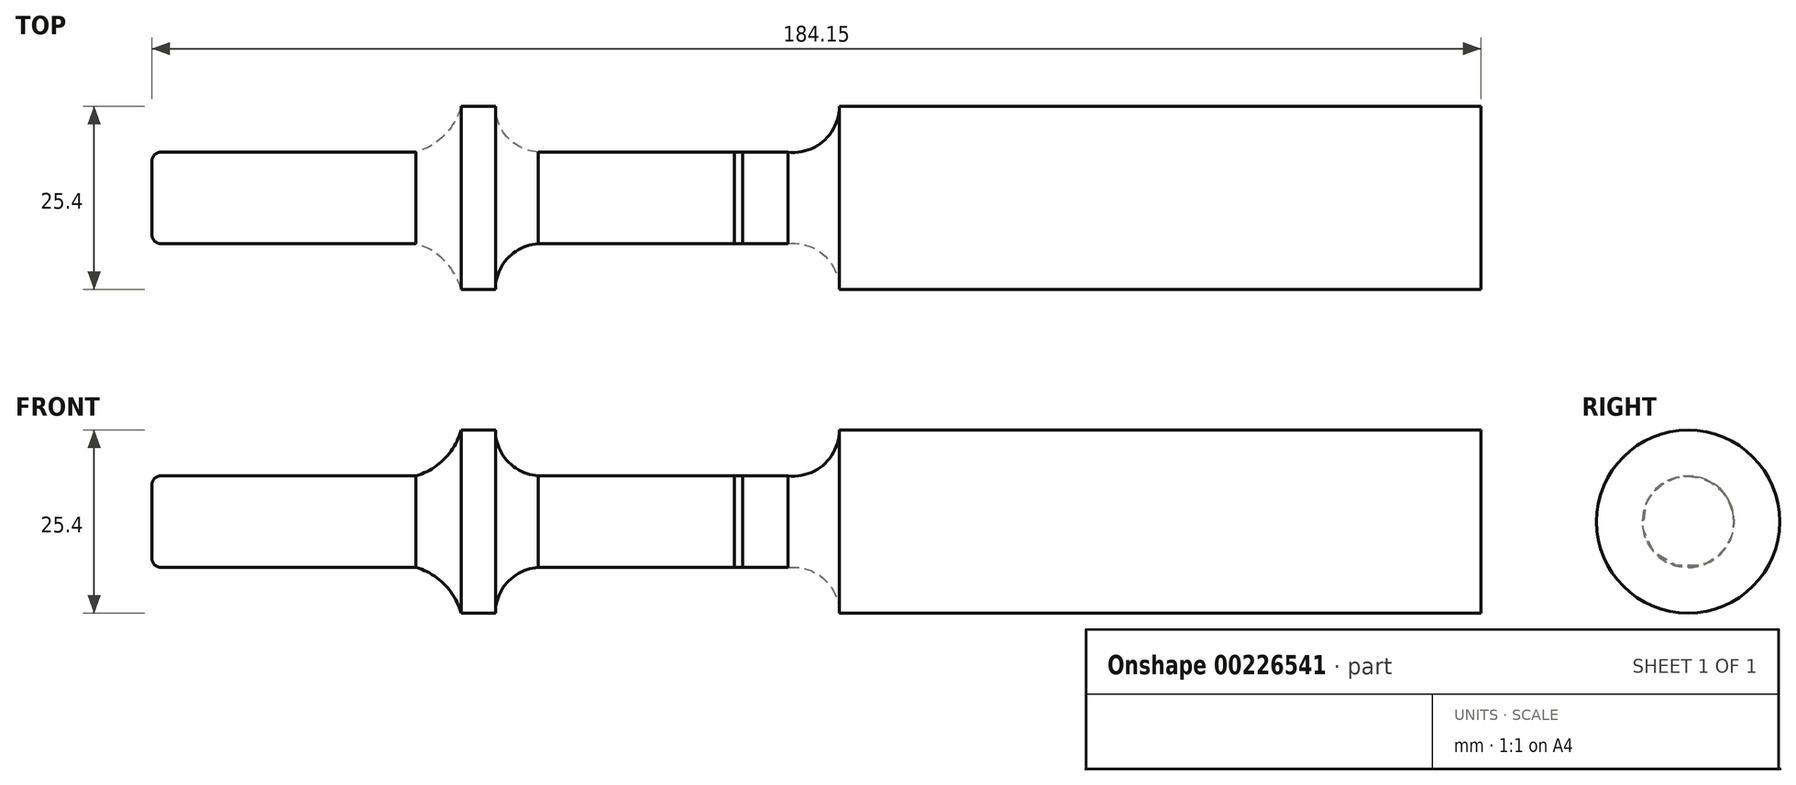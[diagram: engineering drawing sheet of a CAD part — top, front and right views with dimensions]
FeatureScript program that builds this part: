
annotation { "Feature Type Name" : "Feature", "Feature Type Description" : "" }
export const myFeature = defineFeature(function(context is Context, id is Id, definition is map)
    precondition{}
    {
        {
            var Q0;
            Q0=qCreatedBy(makeId("Front.planeOp"),FACE);
            var sketch = newSketch(context, id + "F0", { "sketchPlane" : qUnion([Q0])});
            skLineSegment(sketch, "E0", {"start": v(-80.7, 0) * mm, "end": v(103.46, 0) * mm});
            skLineSegment(sketch, "E1", {"start": v(103.46, 0) * mm, "end": v(103.46, 12.7) * mm});
            skLineSegment(sketch, "E2", {"start": v(-80.7, 0) * mm, "end": v(-80.7, 6.35) * mm});
            skLineSegment(sketch, "E3", {"start": v(103.46, 12.7) * mm, "end": v(20.9, 12.7) * mm});
            skLineSegment(sketch, "E4", {"start": v(-80.7, 6.35) * mm, "end": v(-44.09, 6.35) * mm});
            skLineSegment(sketch, "E5", {"start": v(-37.85, 12.7) * mm, "end": v(-33.1, 12.7) * mm});
            skLineSegment(sketch, "E6", {"start": v(14.56, 6.35) * mm, "end": v(14.56, 6.35) * mm});
            skLineSegment(sketch, "E7", {"start": v(-27.13, 6.35) * mm, "end": v(8.88, 6.35) * mm});
            skPoint(sketch, "E8.visualSharp", {"position": v(14.56, 12.7) * mm});
            skLineSegment(sketch, "E9", {"start": v(14.56, 12.7) * mm, "end": v(20.9, 12.7) * mm});
            skPoint(sketch, "E10", {"position": v(0, 6.35) * mm});
            skArc(sketch, "E11", {"start": v(0, 6.35) * mm, "mid": v(0.58, 6.34) * mm, "end": v(1.17, 6.35) * mm});
            skArc(sketch, "E12", {"start": v(7.45, 6.35) * mm, "mid": v(12.42, 7.94) * mm, "end": v(14.56, 12.7) * mm});
            skArc(sketch, "E13", {"start": v(-44.09, 6.35) * mm, "mid": v(-40.14, 8.72) * mm, "end": v(-37.85, 12.7) * mm});
            skArc(sketch, "E14", {"start": v(-33.1, 12.7) * mm, "mid": v(-31.37, 8.35) * mm, "end": v(-27.13, 6.35) * mm});
            skPoint(sketch, "E15.orphan", {"position": v(-33.1, 6.35) * mm});
            skSolve(sketch);
        }
        {
            var Q0;
            Q0=makeQuery(id+"F0.imprint","IMPRINT",FACE,{"disambiguationData":[TD([[makeQuery(id+"F0.imprint","IMPRINT",EDGE,{"derivedFrom":sQuery(id+"F0.wireOp",EDGE,"E0")}),1.0]])]});
            var Q1;
            Q1=sQuery(id+"F0.wireOp",EDGE,"E0");
            revolve(context, id + "F1", {"entities" : qUnion([Q0]), "axis" : qUnion([Q1]), "revolveType" : RevolveType.FULL});
        }
        {
            var Q0;
            Q0=makeQuery(id+"F1.opRevolve","SWEPT_FACE",FACE,{"disambiguationData":[OSD([sQuery(id+"F0.wireOp",EDGE,"E2")])]});
            fillet(context, id + "F2", {"entities" : qUnion([Q0]), "radius" : 1.27 * mm, "tangentPropagation" : true, "allowEdgeOverflow" : false});
        }
    });
